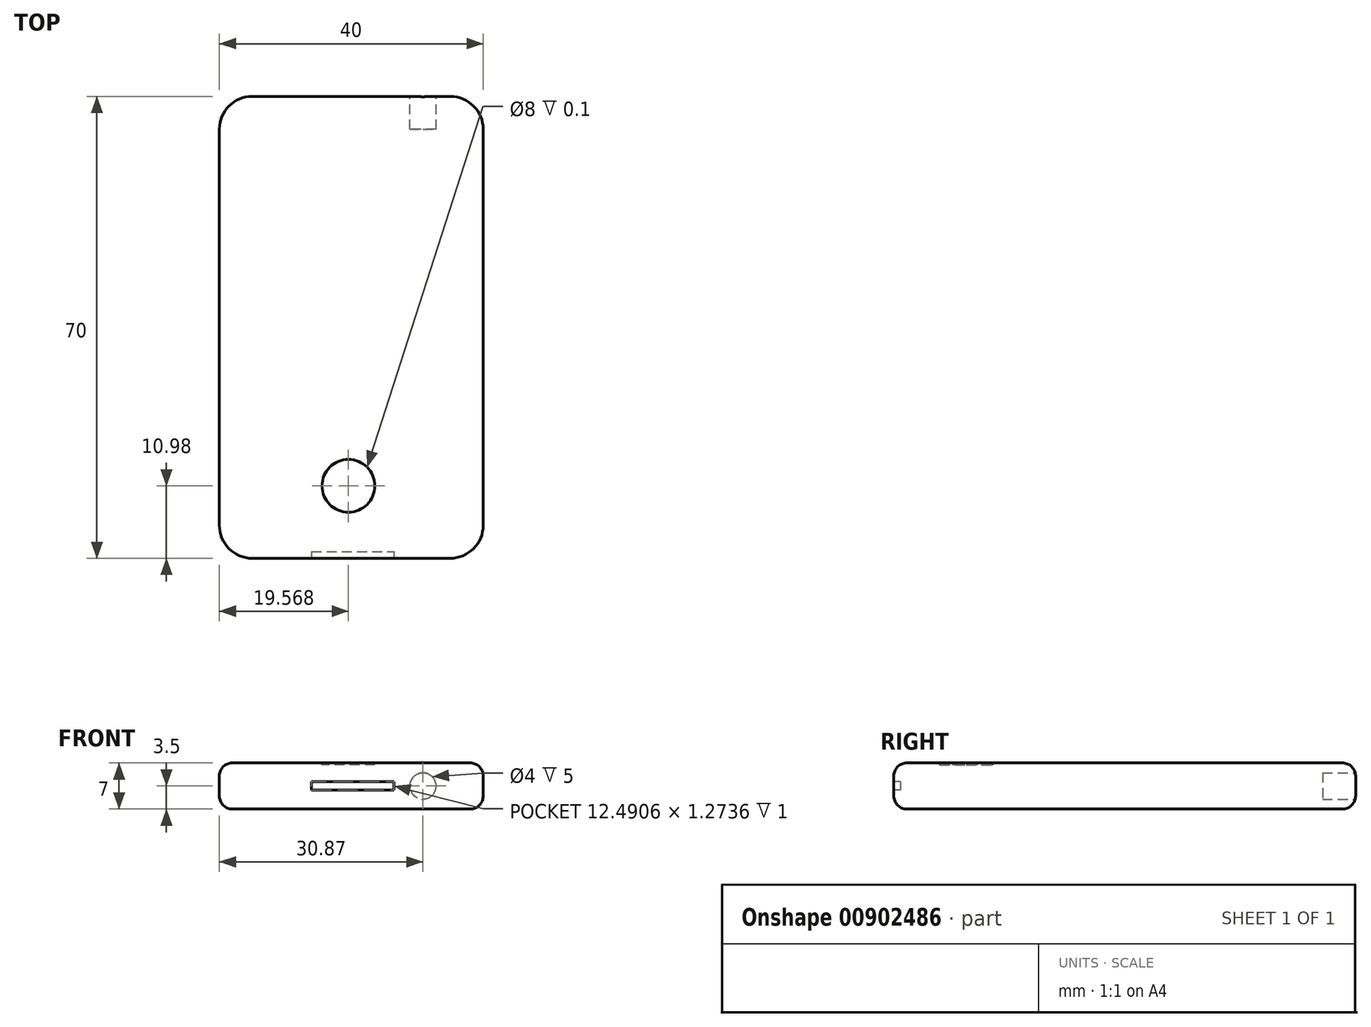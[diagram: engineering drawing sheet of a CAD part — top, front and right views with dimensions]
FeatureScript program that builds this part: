
annotation { "Feature Type Name" : "Feature", "Feature Type Description" : "" }
export const myFeature = defineFeature(function(context is Context, id is Id, definition is map)
    precondition{}
    {
        {
            var Q0;
            Q0=qCreatedBy(makeId("Top.planeOp"),FACE);
            var sketch = newSketch(context, id + "F0", { "sketchPlane" : qUnion([Q0])});
            skLineSegment(sketch, "E0.bottom", {"start": v(0, 0) * mm, "end": v(40, 0) * mm});
            skLineSegment(sketch, "E0.top", {"start": v(0, 70) * mm, "end": v(40, 70) * mm});
            skLineSegment(sketch, "E0.left", {"start": v(0, 0) * mm, "end": v(0, 70) * mm});
            skLineSegment(sketch, "E0.right", {"start": v(40, 0) * mm, "end": v(40, 70) * mm});
            skSolve(sketch);
        }
        {
            var Q0;
            Q0=makeQuery(id+"F0.imprint","IMPRINT",FACE,{"disambiguationData":[TD([[makeQuery(id+"F0.imprint","IMPRINT",EDGE,{"derivedFrom":sQuery(id+"F0.wireOp",EDGE,"E0.bottom")}),1.0]])]});
            extrude(context, id + "F1", {"entities" : qUnion([Q0]), "depth" : 7 * mm, "offsetDistance" : 25 * mm});
        }
        {
            var Q0;
            Q0=makeQuery(id+"F1.opExtrude","SWEPT_EDGE",EDGE,{"disambiguationData":[OSD([sQuery(id+"F0.wireOp",EDGE,"E0.bottom"),sQuery(id+"F0.wireOp",EDGE,"E0.right")])]});
            var Q1;
            Q1=makeQuery(id+"F1.opExtrude","SWEPT_EDGE",EDGE,{"disambiguationData":[OSD([sQuery(id+"F0.wireOp",EDGE,"E0.bottom"),sQuery(id+"F0.wireOp",EDGE,"E0.left")])]});
            var Q2;
            Q2=makeQuery(id+"F1.opExtrude","SWEPT_EDGE",EDGE,{"disambiguationData":[OSD([sQuery(id+"F0.wireOp",EDGE,"E0.top"),sQuery(id+"F0.wireOp",EDGE,"E0.right")])]});
            var Q3;
            Q3=makeQuery(id+"F1.opExtrude","SWEPT_EDGE",EDGE,{"disambiguationData":[OSD([sQuery(id+"F0.wireOp",EDGE,"E0.top"),sQuery(id+"F0.wireOp",EDGE,"E0.left")])]});
            fillet(context, id + "F2", {"entities" : qUnion([Q0, Q1, Q2, Q3]), "radius" : 5 * mm, "tangentPropagation" : true, "allowEdgeOverflow" : false});
        }
        {
            var Q0;
            Q0=makeQuery(id+"F1.opExtrude","SWEPT_FACE",FACE,{"disambiguationData":[OSD([sQuery(id+"F0.wireOp",EDGE,"E0.top")])]});
            var sketch = newSketch(context, id + "F3", { "sketchPlane" : qUnion([Q0])});
            skCircle(sketch, "E1", {"center": v(-30.87, 3.5) * mm, "radius": 2 * mm});
            skPoint(sketch, "E1.centerSnap0", {"position": v(-35, 3.5) * mm});
            skSolve(sketch);
        }
        {
            var Q0;
            Q0 = qSketchRegion(id + "F3", true);
            extrude(context, id + "F4", {"entities" : qUnion([Q0]), "operationType" : NewBodyOperationType.REMOVE, "oppositeDirection" : true, "depth" : 5 * mm, "offsetDistance" : 25 * mm});
        }
        {
            var Q0;
            Q0=makeQuery(id+"F1.opExtrude","CAP_FACE",FACE,{"disambiguationData":[OSD([sQuery(id+"F0.wireOp",EDGE,"E0.bottom"),sQuery(id+"F0.wireOp",EDGE,"E0.top"),sQuery(id+"F0.wireOp",EDGE,"E0.left"),sQuery(id+"F0.wireOp",EDGE,"E0.right")])],"isStart":false});
            var Q1;
            Q1=makeQuery(id+"F1.opExtrude","CAP_FACE",FACE,{"disambiguationData":[OSD([sQuery(id+"F0.wireOp",EDGE,"E0.bottom"),sQuery(id+"F0.wireOp",EDGE,"E0.top"),sQuery(id+"F0.wireOp",EDGE,"E0.left"),sQuery(id+"F0.wireOp",EDGE,"E0.right")])],"isStart":true});
            fillet(context, id + "F5", {"entities" : qUnion([Q0, Q1]), "radius" : 2 * mm, "tangentPropagation" : true, "allowEdgeOverflow" : false});
        }
        {
            var Q0;
            Q0=makeQuery(id+"F1.opExtrude","CAP_FACE",FACE,{"disambiguationData":[OSD([sQuery(id+"F0.wireOp",EDGE,"E0.bottom"),sQuery(id+"F0.wireOp",EDGE,"E0.top"),sQuery(id+"F0.wireOp",EDGE,"E0.left"),sQuery(id+"F0.wireOp",EDGE,"E0.right")])],"isStart":false});
            var sketch = newSketch(context, id + "F6", { "sketchPlane" : qUnion([Q0])});
            skCircle(sketch, "E2", {"center": v(19.57, 10.98) * mm, "radius": 4 * mm});
            skSolve(sketch);
        }
        {
            var Q0;
            Q0 = qSketchRegion(id + "F6", true);
            extrude(context, id + "F7", {"entities" : qUnion([Q0]), "operationType" : NewBodyOperationType.REMOVE, "oppositeDirection" : true, "depth" : 0.3 * mm, "offsetDistance" : 25 * mm});
        }
        {
            var Q0;
            Q0=makeQuery(id+"F7.boolean.opBoolean","COPY",EDGE,{"derivedFrom":makeQuery(id+"F7.opExtrude","CAP_EDGE",EDGE,{"disambiguationData":[OSD([sQuery(id+"F6.wireOp",EDGE,"E2")])],"isStart":true})});
            var Q1;
            Q1=makeQuery(id+"F1.opExtrude","CAP_FACE",FACE,{"disambiguationData":[OSD([sQuery(id+"F0.wireOp",EDGE,"E0.bottom"),sQuery(id+"F0.wireOp",EDGE,"E0.top"),sQuery(id+"F0.wireOp",EDGE,"E0.left"),sQuery(id+"F0.wireOp",EDGE,"E0.right")])],"isStart":false});
            fillet(context, id + "F8", {"entities" : qUnion([Q0, Q1]), "radius" : 0.2 * mm, "tangentPropagation" : true, "allowEdgeOverflow" : false});
        }
        {
            var Q0;
            Q0=makeQuery(id+"F1.opExtrude","SWEPT_FACE",FACE,{"disambiguationData":[OSD([sQuery(id+"F0.wireOp",EDGE,"E0.bottom")])]});
            var sketch = newSketch(context, id + "F9", { "sketchPlane" : qUnion([Q0])});
            skLineSegment(sketch, "E3.bottom", {"start": v(13.98, 4.18) * mm, "end": v(26.47, 4.18) * mm});
            skLineSegment(sketch, "E3.top", {"start": v(13.98, 2.9) * mm, "end": v(26.47, 2.9) * mm});
            skLineSegment(sketch, "E3.left", {"start": v(13.98, 4.18) * mm, "end": v(13.98, 2.9) * mm});
            skLineSegment(sketch, "E3.right", {"start": v(26.47, 4.18) * mm, "end": v(26.47, 2.9) * mm});
            skSolve(sketch);
        }
        {
            var Q0;
            Q0 = qSketchRegion(id + "F9", true);
            extrude(context, id + "F10", {"entities" : qUnion([Q0]), "operationType" : NewBodyOperationType.REMOVE, "oppositeDirection" : true, "depth" : 1 * mm, "offsetDistance" : 25 * mm});
        }
    });
